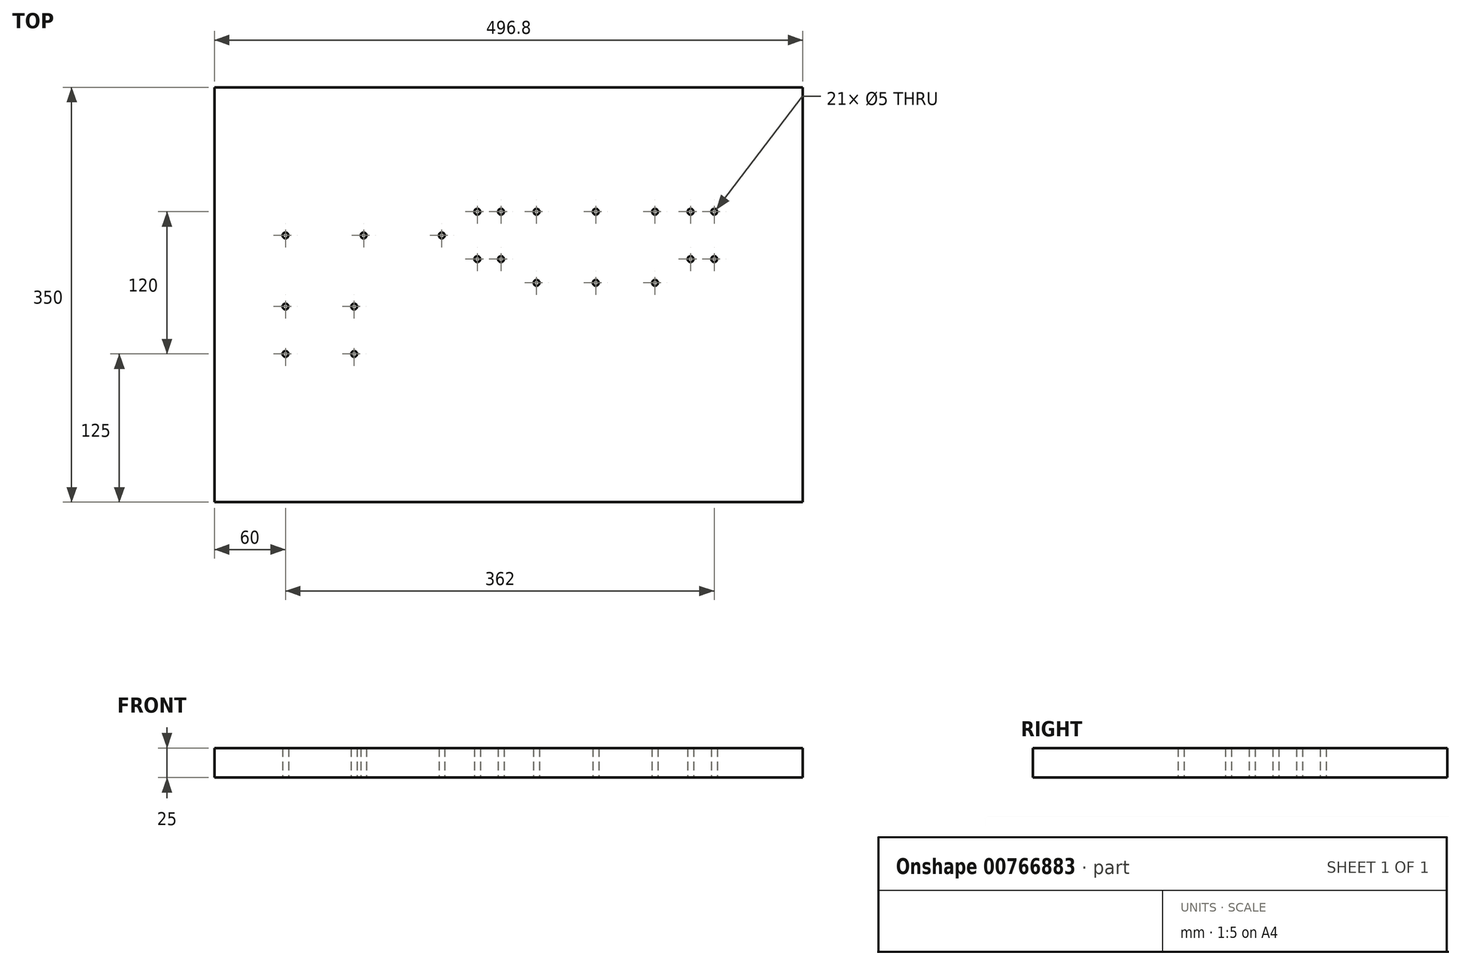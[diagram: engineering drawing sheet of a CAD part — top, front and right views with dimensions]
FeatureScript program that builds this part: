
annotation { "Feature Type Name" : "Feature", "Feature Type Description" : "" }
export const myFeature = defineFeature(function(context is Context, id is Id, definition is map)
    precondition{}
    {
        {
            var Q0;
            Q0=qCreatedBy(makeId("Top.planeOp"),FACE);
            var sketch = newSketch(context, id + "F0", { "sketchPlane" : qUnion([Q0])});
            skLineSegment(sketch, "E0.bottom", {"start": v(0, 0) * mm, "end": v(496.8, 0) * mm});
            skLineSegment(sketch, "E0.top", {"start": v(0, 350) * mm, "end": v(496.8, 350) * mm});
            skLineSegment(sketch, "E0.left", {"start": v(0, 0) * mm, "end": v(0, 350) * mm});
            skLineSegment(sketch, "E0.right", {"start": v(496.8, 0) * mm, "end": v(496.8, 350) * mm});
            skCircle(sketch, "E1", {"center": v(60, 125) * mm, "radius": 2.5 * mm});
            skCircle(sketch, "E2", {"center": v(118, 125) * mm, "radius": 2.5 * mm});
            skCircle(sketch, "E3", {"center": v(118, 165) * mm, "radius": 2.5 * mm});
            skCircle(sketch, "E4", {"center": v(60, 165) * mm, "radius": 2.5 * mm});
            skCircle(sketch, "E5", {"center": v(60, 225) * mm, "radius": 2.5 * mm});
            skCircle(sketch, "E6", {"center": v(126, 225) * mm, "radius": 2.5 * mm});
            skCircle(sketch, "E7", {"center": v(192, 225) * mm, "radius": 2.5 * mm});
            skCircle(sketch, "E8", {"center": v(222, 245) * mm, "radius": 2.5 * mm});
            skCircle(sketch, "E9", {"center": v(242, 245) * mm, "radius": 2.5 * mm});
            skCircle(sketch, "E10", {"center": v(242, 205) * mm, "radius": 2.5 * mm});
            skCircle(sketch, "E11", {"center": v(222, 205) * mm, "radius": 2.5 * mm});
            skCircle(sketch, "E12", {"center": v(272, 245) * mm, "radius": 2.5 * mm});
            skCircle(sketch, "E13", {"center": v(322, 245) * mm, "radius": 2.5 * mm});
            skCircle(sketch, "E14", {"center": v(322, 185) * mm, "radius": 2.5 * mm});
            skCircle(sketch, "E15", {"center": v(272, 185) * mm, "radius": 2.5 * mm});
            skCircle(sketch, "E16", {"center": v(372, 245) * mm, "radius": 2.5 * mm});
            skCircle(sketch, "E17", {"center": v(372, 185) * mm, "radius": 2.5 * mm});
            skCircle(sketch, "E18", {"center": v(402, 245) * mm, "radius": 2.5 * mm});
            skCircle(sketch, "E19", {"center": v(422, 245) * mm, "radius": 2.5 * mm});
            skCircle(sketch, "E20", {"center": v(402, 205) * mm, "radius": 2.5 * mm});
            skCircle(sketch, "E21", {"center": v(422, 205) * mm, "radius": 2.5 * mm});
            skSolve(sketch);
        }
        {
            var Q0;
            Q0=makeQuery(id+"F0.imprint","IMPRINT",FACE,{"disambiguationData":[TD([[makeQuery(id+"F0.imprint","IMPRINT",EDGE,{"derivedFrom":sQuery(id+"F0.wireOp",EDGE,"E0.bottom")}),1.0]])]});
            extrude(context, id + "F1", {"entities" : qUnion([Q0]), "depth" : 25 * mm, "offsetDistance" : 25 * mm});
        }
    });
